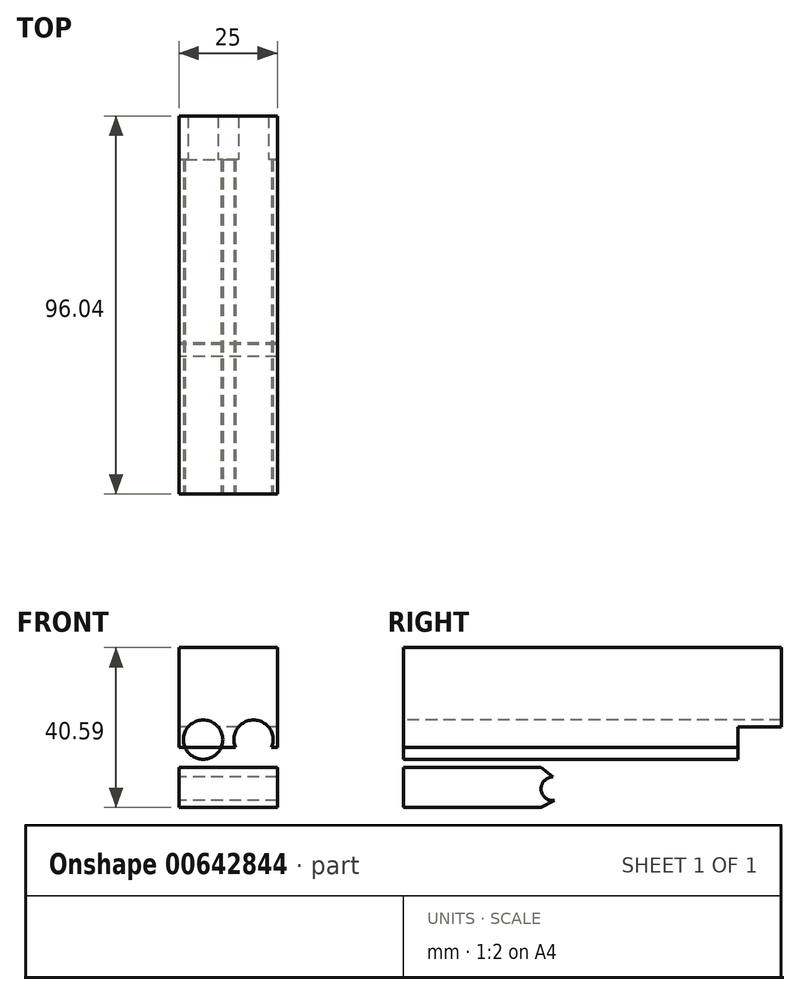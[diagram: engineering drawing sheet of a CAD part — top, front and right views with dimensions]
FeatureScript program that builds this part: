
annotation { "Feature Type Name" : "Feature", "Feature Type Description" : "" }
export const myFeature = defineFeature(function(context is Context, id is Id, definition is map)
    precondition{}
    {
        {
            var Q0;
            Q0=qCreatedBy(makeId("Right.planeOp"),FACE);
            var sketch = newSketch(context, id + "F0", { "sketchPlane" : qUnion([Q0])});
            skLineSegment(sketch, "E0.bottom", {"start": v(0, 0) * mm, "end": v(60, 0) * mm});
            skLineSegment(sketch, "E0.top", {"start": v(0, 10.2) * mm, "end": v(60, 10.2) * mm});
            skLineSegment(sketch, "E0.left", {"start": v(0, 0) * mm, "end": v(0, 10.2) * mm});
            skLineSegment(sketch, "E0.right", {"start": v(60, 0) * mm, "end": v(60, 10.2) * mm});
            skLineSegment(sketch, "E1.bottom", {"start": v(0, 10.2) * mm, "end": v(71.04, 10.2) * mm});
            skLineSegment(sketch, "E1.top", {"start": v(0, 30.4) * mm, "end": v(71.04, 30.4) * mm});
            skLineSegment(sketch, "E1.left", {"start": v(0, 10.2) * mm, "end": v(0, 30.4) * mm});
            skLineSegment(sketch, "E1.right", {"start": v(71.04, 10.2) * mm, "end": v(71.04, 30.4) * mm});
            skLineSegment(sketch, "E2", {"start": v(0, 0) * mm, "end": v(0, -10.2) * mm});
            skLineSegment(sketch, "E3", {"start": v(0, -10.2) * mm, "end": v(10, -10.2) * mm});
            skLineSegment(sketch, "E4", {"start": v(10, -10.2) * mm, "end": v(10, 0) * mm});
            skArc(sketch, "E5", {"start": v(12.98, -2.48) * mm, "mid": v(10, -5.7) * mm, "end": v(13.44, -8.45) * mm});
            skLineSegment(sketch, "E6", {"start": v(12.98, -2.48) * mm, "end": v(10, 0) * mm});
            skLineSegment(sketch, "E7", {"start": v(10, -10.2) * mm, "end": v(13.44, -8.45) * mm});
            skSolve(sketch);
        }
        {
            var Q0;
            Q0 = qSketchRegion(id + "F0", true);
            extrude(context, id + "F1", {"entities" : qUnion([Q0]), "depth" : 25 * mm, "offsetDistance" : 25 * mm});
        }
        {
            var Q0;
            Q0=makeQuery(id+"F1.opExtrude","SWEPT_FACE",FACE,{"disambiguationData":[OSD([sQuery(id+"F0.wireOp",EDGE,"E0.left"),sQuery(id+"F0.wireOp",EDGE,"E1.left"),sQuery(id+"F0.wireOp",EDGE,"E2")])]});
            var sketch = newSketch(context, id + "F2", { "sketchPlane" : qUnion([Q0])});
            skLineSegment(sketch, "E8", {"start": v(0, 0) * mm, "end": v(25, 0) * mm});
            skLineSegment(sketch, "E9", {"start": v(25, 0) * mm, "end": v(25, 10) * mm});
            skLineSegment(sketch, "E10", {"start": v(25, 10) * mm, "end": v(0, 10) * mm});
            skLineSegment(sketch, "E11", {"start": v(0, 10) * mm, "end": v(0, 0) * mm});
            skLineSegment(sketch, "E12", {"start": v(0, 5) * mm, "end": v(25, 5) * mm});
            skCircle(sketch, "E13", {"center": v(6.16, 7) * mm, "radius": 5 * mm});
            skCircle(sketch, "E14", {"center": v(18.96, 7) * mm, "radius": 5 * mm});
            skSolve(sketch);
        }
        {
            var Q0;
            {var subQ0=sQuery(id+"F2.wireOp",EDGE,"E13");var subQ1=sQuery(id+"F2.wireOp",EDGE,"E10");var subQ2=makeQuery(id+"F2.imprint","INTERSECT",VERTEX,{"disambiguationData":[OD(0.0)],"derivedFrom":[subQ1,subQ0]});Q0=makeQuery(id+"F2.imprint","IMPRINT",FACE,{"disambiguationData":[TD([[makeQuery(id+"F2.imprint","IMPRINT",EDGE,{"disambiguationData":[TD([[subQ2,-1.0]])],"derivedFrom":subQ1}),-1.0]])]});}
            var Q1;
            {var subQ0=sQuery(id+"F2.wireOp",EDGE,"E13");var subQ1=sQuery(id+"F2.wireOp",EDGE,"E10");var subQ2=makeQuery(id+"F2.imprint","INTERSECT",VERTEX,{"disambiguationData":[OD(0.0)],"derivedFrom":[subQ1,subQ0]});Q1=makeQuery(id+"F2.imprint","IMPRINT",FACE,{"disambiguationData":[TD([[makeQuery(id+"F2.imprint","IMPRINT",EDGE,{"disambiguationData":[TD([[subQ2,-1.0]])],"derivedFrom":subQ1}),1.0]])]});}
            var Q2;
            {var subQ0=sQuery(id+"F2.wireOp",EDGE,"E13");var subQ1=sQuery(id+"F2.wireOp",EDGE,"E12");var subQ2=makeQuery(id+"F2.imprint","INTERSECT",VERTEX,{"disambiguationData":[OD(0.0)],"derivedFrom":[subQ1,subQ0]});Q2=makeQuery(id+"F2.imprint","IMPRINT",FACE,{"disambiguationData":[TD([[makeQuery(id+"F2.imprint","IMPRINT",EDGE,{"disambiguationData":[TD([[subQ2,-1.0]])],"derivedFrom":subQ1}),-1.0]])]});}
            var Q3;
            {var subQ0=sQuery(id+"F2.wireOp",EDGE,"E14");var subQ1=sQuery(id+"F2.wireOp",EDGE,"E10");var subQ2=makeQuery(id+"F2.imprint","INTERSECT",VERTEX,{"disambiguationData":[OD(0.0)],"derivedFrom":[subQ1,subQ0]});Q3=makeQuery(id+"F2.imprint","IMPRINT",FACE,{"disambiguationData":[TD([[makeQuery(id+"F2.imprint","IMPRINT",EDGE,{"disambiguationData":[TD([[subQ2,-1.0]])],"derivedFrom":subQ1}),-1.0]])]});}
            var Q4;
            {var subQ0=sQuery(id+"F2.wireOp",EDGE,"E14");var subQ1=sQuery(id+"F2.wireOp",EDGE,"E10");var subQ2=makeQuery(id+"F2.imprint","INTERSECT",VERTEX,{"disambiguationData":[OD(0.0)],"derivedFrom":[subQ1,subQ0]});Q4=makeQuery(id+"F2.imprint","IMPRINT",FACE,{"disambiguationData":[TD([[makeQuery(id+"F2.imprint","IMPRINT",EDGE,{"disambiguationData":[TD([[subQ2,-1.0]])],"derivedFrom":subQ1}),1.0]])]});}
            var Q5;
            {var subQ0=sQuery(id+"F2.wireOp",EDGE,"E14");var subQ1=sQuery(id+"F2.wireOp",EDGE,"E12");var subQ2=makeQuery(id+"F2.imprint","INTERSECT",VERTEX,{"disambiguationData":[OD(0.0)],"derivedFrom":[subQ1,subQ0]});Q5=makeQuery(id+"F2.imprint","IMPRINT",FACE,{"disambiguationData":[TD([[makeQuery(id+"F2.imprint","IMPRINT",EDGE,{"disambiguationData":[TD([[subQ2,-1.0]])],"derivedFrom":subQ1}),-1.0]])]});}
            extrude(context, id + "F3", {"entities" : qUnion([Q0, Q1, Q2, Q3, Q4, Q5]), "operationType" : NewBodyOperationType.REMOVE, "endBound" : BoundingType.THROUGH_ALL, "oppositeDirection" : true, "depth" : 25 * mm, "offsetDistance" : 25 * mm});
        }
        {
            var Q0;
            Q0=makeQuery(id+"F1.opExtrude","SWEPT_FACE",FACE,{"disambiguationData":[OSD([sQuery(id+"F0.wireOp",EDGE,"E0.left"),sQuery(id+"F0.wireOp",EDGE,"E1.left"),sQuery(id+"F0.wireOp",EDGE,"E2")])]});
            extrude(context, id + "F4", {"entities" : qUnion([Q0]), "operationType" : NewBodyOperationType.ADD, "depth" : 25 * mm, "offsetDistance" : 25 * mm});
        }
    });
